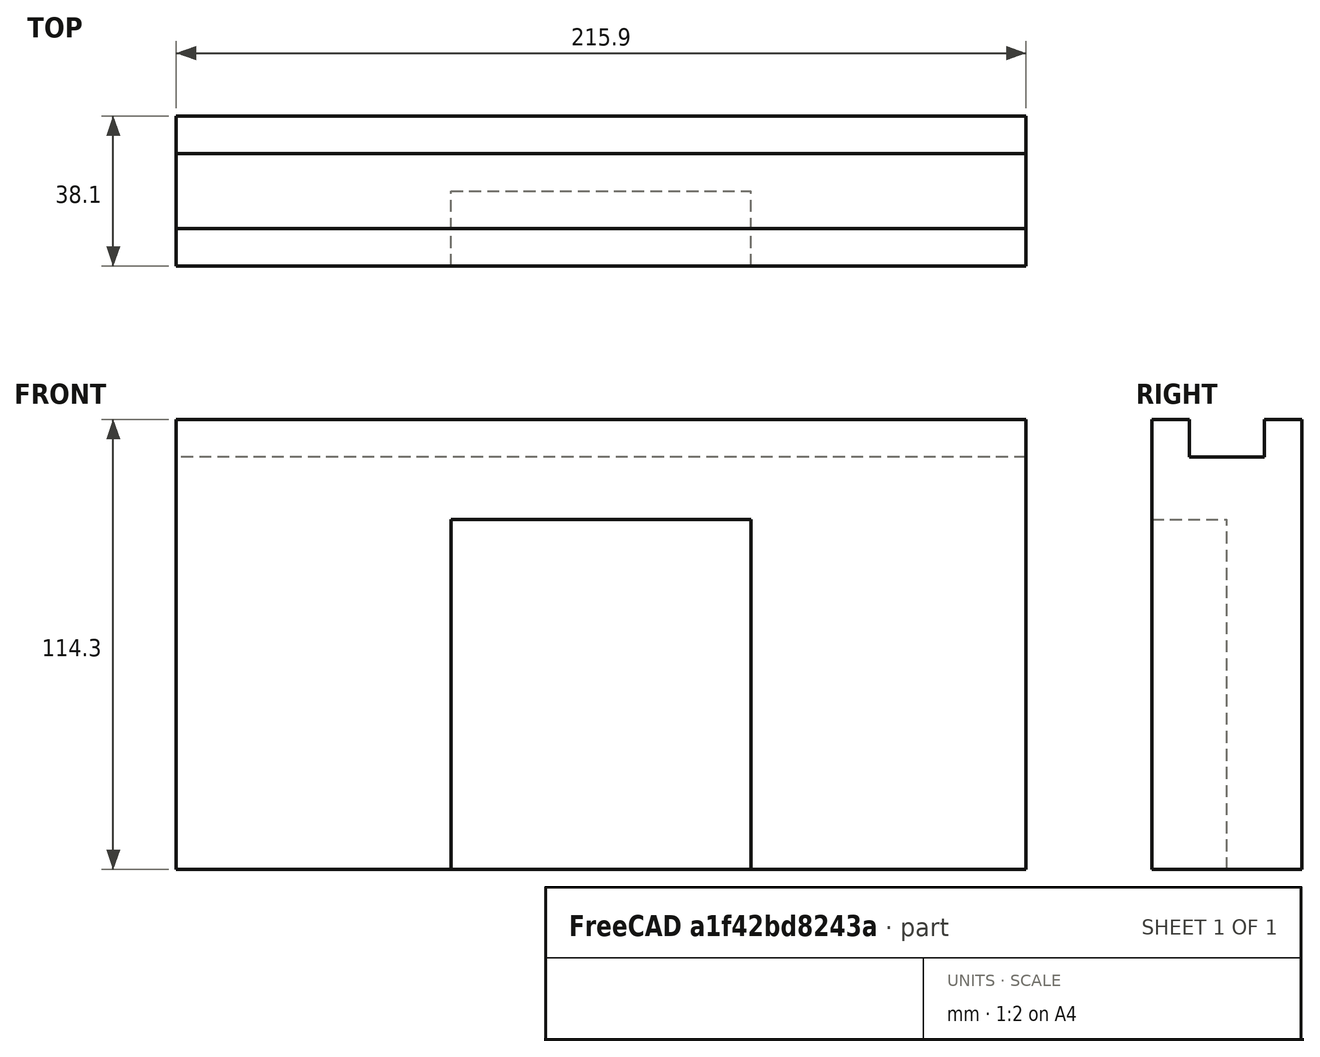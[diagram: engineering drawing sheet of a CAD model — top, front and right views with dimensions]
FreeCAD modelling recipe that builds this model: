
FCSTD DOCUMENT  (FreeCAD 0.20R29603 (Git))
Label: far_fence
License: All rights reserved
LicenseURL: http://en.wikipedia.org/wiki/All_rights_reserved
objects: TechDraw::DrawViewDimension×8, Sketcher::SketchObject×3, TechDraw::DrawProjGroupItem×3, PartDesign::Pocket×2, PartDesign::Pad×1, PartDesign::Body×1, App::Part×1, TechDraw::DrawSVGTemplate×1, TechDraw::DrawProjGroup×1, TechDraw::DrawViewSection×1, TechDraw::DrawPage×1
note: 10 computed .brp shape members not serialized (recipe doc carries the construction recipe); baked Part::Feature solids carry a one-line shape summary decoded from their .brp

FEATURE [Sketcher::SketchObject] Sketch
  FullyConstrained = true
  MapMode = 5
  Support = -> [XY_Plane002]
  sketch-geometry (5):
    g0: LineSegment StartX=-107.95 StartY=-19.05 StartZ=0 EndX=-107.95 EndY=19.05 EndZ=0
    g1: LineSegment StartX=-107.95 StartY=19.05 StartZ=0 EndX=107.95 EndY=19.05 EndZ=0
    g2: LineSegment StartX=107.95 StartY=19.05 StartZ=0 EndX=107.95 EndY=-19.05 EndZ=0
    g3: LineSegment StartX=107.95 StartY=-19.05 StartZ=0 EndX=-107.95 EndY=-19.05 EndZ=0
    g4: GeomPoint X=0 Y=0 Z=0
  constraints (12):
    c: Coincident(g0,g1)
    c: Coincident(g1,g2)
    c: Coincident(g2,g3)
    c: Coincident(g3,g0)
    c: Horizontal(g1)
    c: Horizontal(g3)
    c: Vertical(g0)
    c: Vertical(g2)
    c: Symmetric(g1,g0,g4)
    c: Coincident(g4,g-1)
    c: DistanceX(g1,g1) = 215.9
    c: DistanceY(g2,g2) = 38.1
FEATURE [PartDesign::Pad] Pad  label="Base"
  Direction = (0,0,1)
  Length = 114.3
  Length2 = 10
  Profile = -> Sketch
  ReferenceAxis = -> Sketch [N_Axis]
  Type = 0
FEATURE [Sketcher::SketchObject] Sketch001
  ExternalGeometry = -> [Pad]
  FullyConstrained = false
  MapMode = 5
  Placement = pos=(0,0,114.3) rot=(0,0,1;0rad)
  Support = -> [Pad]
  sketch-geometry (5):
    g0: LineSegment StartX=381 StartY=-9.525 StartZ=0 EndX=381 EndY=9.525 EndZ=0
    g1: LineSegment StartX=381 StartY=9.525 StartZ=0 EndX=-381 EndY=9.525 EndZ=0
    g2: LineSegment StartX=-381 StartY=9.525 StartZ=0 EndX=-381 EndY=-9.525 EndZ=0
    g3: LineSegment StartX=-381 StartY=-9.525 StartZ=0 EndX=381 EndY=-9.525 EndZ=0
    g4: GeomPoint X=-1.77e-14 Y=-1e-16 Z=0
  constraints (11):
    c: Coincident(g0,g1)
    c: Coincident(g1,g2)
    c: Coincident(g2,g3)
    c: Coincident(g3,g0)
    c: Horizontal(g1)
    c: Horizontal(g3)
    c: Symmetric(g1,g0,g4)
    c: Tangent(g-3,g2)
    c: Tangent(g0,g-4)
    c: Coincident(g4,g-1)
    c: DistanceY(g2,g2) = 19.05
FEATURE [PartDesign::Pocket] Pocket  label="Top T-Track Dado"
  BaseFeature = -> Pad
  Direction = (0,0,-1)
  Length = 9.525
  Length2 = 5
  Profile = -> Sketch001
  ReferenceAxis = -> Sketch001 [N_Axis]
  Type = 0
FEATURE [Sketcher::SketchObject] Sketch003
  ExternalGeometry = -> [Pocket]
  FullyConstrained = true
  MapMode = 5
  Placement = pos=(0,-19.05,0) rot=(1,0,0;1.5708rad)
  sketch-geometry (5):
    g0: LineSegment StartX=-38.1 StartY=88.9 StartZ=0 EndX=-38.1 EndY=0 EndZ=0
    g1: LineSegment StartX=-38.1 StartY=0 StartZ=0 EndX=38.1 EndY=0 EndZ=0
    g2: LineSegment StartX=38.1 StartY=0 StartZ=0 EndX=38.1 EndY=88.9 EndZ=0
    g3: LineSegment StartX=38.1 StartY=88.9 StartZ=0 EndX=-38.1 EndY=88.9 EndZ=0
    g4: GeomPoint X=0 Y=44.45 Z=0
  constraints (12):
    c: Coincident(g0,g1)
    c: Coincident(g1,g2)
    c: Coincident(g2,g3)
    c: Coincident(g3,g0)
    c: Horizontal(g3)
    c: Vertical(g0)
    c: Vertical(g2)
    c: Symmetric(g1,g0,g4)
    c: PointOnObject(g4,g-2)
    c: DistanceY(g0,g0) = 88.9
    c: DistanceX(g3,g3) = 76.2
    c: Tangent(g1,g-3)
FEATURE [PartDesign::Pocket] Pocket002
  BaseFeature = -> Pocket
  Direction = (0,1,-2e-16)
  Length = 19.05
  Length2 = 5
  Profile = -> Sketch003
  ReferenceAxis = -> Sketch003 [N_Axis]
  Type = 0
FEATURE [PartDesign::Body] PocketBody
  Group = -> [Sketch,Pad,Sketch001,Pocket,Sketch003,Pocket002]
  Origin = -> Origin002
  Tip = -> Pocket002
FEATURE [App::Part] Part
  Group = -> [PocketBody]
  Origin = -> Origin001
FEATURE [TechDraw::DrawSVGTemplate] Template
  Height = 297
  Orientation = 1
  Width = 420
FEATURE [TechDraw::DrawProjGroupItem] ProjItem  label="Front"
  CoarseView = false
  Direction = (0,-1,0)
  Focus = 100
  HardHidden = false
  IsoCount = 0
  IsoHidden = false
  IsoVisible = false
  LockPosition = true
  Perspective = false
  Rotation = 0
  RotationVector = (1,0,0)
  Scale = 0.5
  ScaleType = 2
  SeamHidden = false
  SeamVisible = true
  SmoothHidden = false
  SmoothVisible = true
  Source = -> [Part]
  Type = 0
  X = 0
  XDirection = (1,0,0)
  Y = 0
FEATURE [TechDraw::DrawProjGroupItem] ProjItem001  label="FrontTopRight"
  CoarseView = false
  Direction = (0.57735,-0.57735,0.57735)
  Focus = 100
  HardHidden = false
  IsoCount = 0
  IsoHidden = false
  IsoVisible = false
  LockPosition = false
  Perspective = false
  Rotation = 0
  RotationVector = (1,0,0)
  Scale = 0.5
  ScaleType = 2
  SeamHidden = false
  SeamVisible = true
  SmoothHidden = false
  SmoothVisible = true
  Source = -> [Part]
  Type = 7
  X = 123.031
  XDirection = (0.707107,0.707107,0)
  Y = 123.031
FEATURE [TechDraw::DrawProjGroupItem] ProjItem002  label="Left"
  CoarseView = false
  Direction = (-1,-1e-16,0)
  Focus = 100
  HardHidden = false
  IsoCount = 0
  IsoHidden = false
  IsoVisible = false
  LockPosition = false
  Perspective = false
  Rotation = 0
  RotationVector = (1,0,0)
  Scale = 0.5
  ScaleType = 2
  SeamHidden = false
  SeamVisible = true
  SmoothHidden = false
  SmoothVisible = true
  Source = -> [Part]
  Type = 1
  X = -123.031
  XDirection = (1e-16,-1,0)
  Y = 0
FEATURE [TechDraw::DrawProjGroup] ProjGroup
  Anchor = -> ProjItem
  AutoDistribute = true
  LockPosition = false
  ProjectionType = 1
  Rotation = 0
  Scale = 0.5
  ScaleType = 0
  Source = -> [Part]
  Views = -> [ProjItem,ProjItem001,ProjItem002]
  X = 226.932
  Y = 131.048
  spacingX = 15.0812
  spacingY = 15.0812
FEATURE [TechDraw::DrawViewSection] SectionView  label="Section  - "
  BaseView = -> ProjItem
  CoarseView = false
  CutSurfaceDisplay = 2
  Direction = (-1,0,0)
  FileGeomPattern = <path>
  FileHatchPattern = <path>
  Focus = 100
  FuseBeforeCut = false
  HardHidden = false
  HatchScale = 1
  IsoCount = 0
  IsoHidden = false
  IsoVisible = false
  LockPosition = false
  NameGeomPattern = Diamond
  Perspective = false
  Rotation = 0
  Scale = 0.5
  ScaleType = 2
  SeamHidden = false
  SeamVisible = true
  SectionDirection = 0
  SectionNormal = (-1,0,0)
  SectionOrigin = (0,0,57.15)
  SmoothHidden = false
  SmoothVisible = true
  Source = -> [Part]
  X = 336.683
  XDirection = (0,-1,0)
  Y = 130.016
FEATURE [TechDraw::DrawViewDimension] Dimension
  AngleOverride = false
  Arbitrary = false
  ArbitraryTolerances = false
  EqualTolerance = true
  ExtensionAngle = 0
  FormatSpec = %.2w
  FormatSpecOverTolerance = %+.2w
  FormatSpecUnderTolerance = %+.2w
  Inverted = false
  LineAngle = 0
  LockPosition = false
  MeasureType = 1
  OverTolerance = 0
  References2D = -> [ProjItem002]
  Rotation = 0
  Scale = 0.5
  ScaleType = 0
  TheoreticalExact = false
  Type = 1
  UnderTolerance = 0
  X = -51.6133
  Y = -52.5289
FEATURE [TechDraw::DrawViewDimension] Dimension001
  AngleOverride = false
  Arbitrary = false
  ArbitraryTolerances = false
  EqualTolerance = true
  ExtensionAngle = 0
  FormatSpec = %.2w
  FormatSpecOverTolerance = %+.2w
  FormatSpecUnderTolerance = %+.2w
  Inverted = false
  LineAngle = 0
  LockPosition = false
  MeasureType = 1
  OverTolerance = 0
  References2D = -> [ProjItem]
  Rotation = 0
  Scale = 0.5
  ScaleType = 0
  TheoreticalExact = false
  Type = 2
  UnderTolerance = 0
  X = -84.1405
  Y = 3.51176
FEATURE [TechDraw::DrawViewDimension] Dimension002
  AngleOverride = false
  Arbitrary = false
  ArbitraryTolerances = false
  EqualTolerance = true
  ExtensionAngle = 0
  FormatSpec = %.2w
  FormatSpecOverTolerance = %+.2w
  FormatSpecUnderTolerance = %+.2w
  Inverted = false
  LineAngle = 0
  LockPosition = false
  MeasureType = 1
  OverTolerance = 0
  References2D = -> [ProjItem]
  Rotation = 0
  Scale = 0.5
  ScaleType = 0
  TheoreticalExact = false
  Type = 1
  UnderTolerance = 0
  X = -2.65444
  Y = 50.7312
FEATURE [TechDraw::DrawViewDimension] Dimension003
  AngleOverride = false
  Arbitrary = false
  ArbitraryTolerances = false
  EqualTolerance = true
  ExtensionAngle = 0
  FormatSpec = %.2w
  FormatSpecOverTolerance = %+.2w
  FormatSpecUnderTolerance = %+.2w
  Inverted = false
  LineAngle = 0
  LockPosition = false
  MeasureType = 1
  OverTolerance = 0
  References2D = -> [ProjItem]
  Rotation = 0
  Scale = 0.5
  ScaleType = 0
  TheoreticalExact = false
  Type = 2
  UnderTolerance = 0
  X = -68.5465
  Y = -5.76114
FEATURE [TechDraw::DrawViewDimension] Dimension004
  AngleOverride = false
  Arbitrary = false
  ArbitraryTolerances = false
  EqualTolerance = true
  ExtensionAngle = 0
  FormatSpec = %.2w
  FormatSpecOverTolerance = %+.2w
  FormatSpecUnderTolerance = %+.2w
  Inverted = false
  LineAngle = 0
  LockPosition = false
  MeasureType = 1
  OverTolerance = 0
  References2D = -> [ProjItem]
  Rotation = 0
  Scale = 0.5
  ScaleType = 0
  TheoreticalExact = false
  Type = 1
  UnderTolerance = 0
  X = -0.331805
  Y = -45.9155
FEATURE [TechDraw::DrawViewDimension] Dimension005
  AngleOverride = false
  Arbitrary = false
  ArbitraryTolerances = false
  EqualTolerance = true
  ExtensionAngle = 0
  FormatSpec = %.2w
  FormatSpecOverTolerance = %+.2w
  FormatSpecUnderTolerance = %+.2w
  Inverted = false
  LineAngle = 0
  LockPosition = false
  MeasureType = 1
  OverTolerance = 0
  References2D = -> [SectionView]
  Rotation = 0
  Scale = 0.5
  ScaleType = 0
  TheoreticalExact = false
  Type = 1
  UnderTolerance = 0
  X = 26.9748
  Y = -45.1787
FEATURE [TechDraw::DrawViewDimension] Dimension006
  AngleOverride = false
  Arbitrary = false
  ArbitraryTolerances = false
  EqualTolerance = true
  ExtensionAngle = 0
  FormatSpec = %.2w
  FormatSpecOverTolerance = %+.2w
  FormatSpecUnderTolerance = %+.2w
  Inverted = false
  LineAngle = 0
  LockPosition = false
  MeasureType = 1
  OverTolerance = 0
  References2D = -> [ProjItem002]
  Rotation = 0
  Scale = 0.5
  ScaleType = 0
  TheoreticalExact = false
  Type = 1
  UnderTolerance = 0
  X = 0.420688
  Y = 55.63
FEATURE [TechDraw::DrawViewDimension] Dimension007
  AngleOverride = false
  Arbitrary = false
  ArbitraryTolerances = false
  EqualTolerance = true
  ExtensionAngle = 0
  FormatSpec = %.2w
  FormatSpecOverTolerance = %+.2w
  FormatSpecUnderTolerance = %+.2w
  Inverted = false
  LineAngle = 0
  LockPosition = false
  MeasureType = 1
  OverTolerance = 0
  References2D = -> [ProjItem002]
  Rotation = 0
  Scale = 0.5
  ScaleType = 0
  TheoreticalExact = false
  Type = 2
  UnderTolerance = 0
  X = -45.9899
  Y = 14.4701
FEATURE [TechDraw::DrawPage] Page
  KeepUpdated = true
  NextBalloonIndex = 1
  ProjectionType = 0
  Scale = 0.5
  Template = -> Template
  Views = -> [ProjGroup,SectionView,Dimension,Dimension001,Dimension002,Dimension003,Dimension004,Dimension005,Dimension006,Dimension007]
note: 2 file-system paths scrubbed to <path> (originals preserved in the JSON sidecar)
